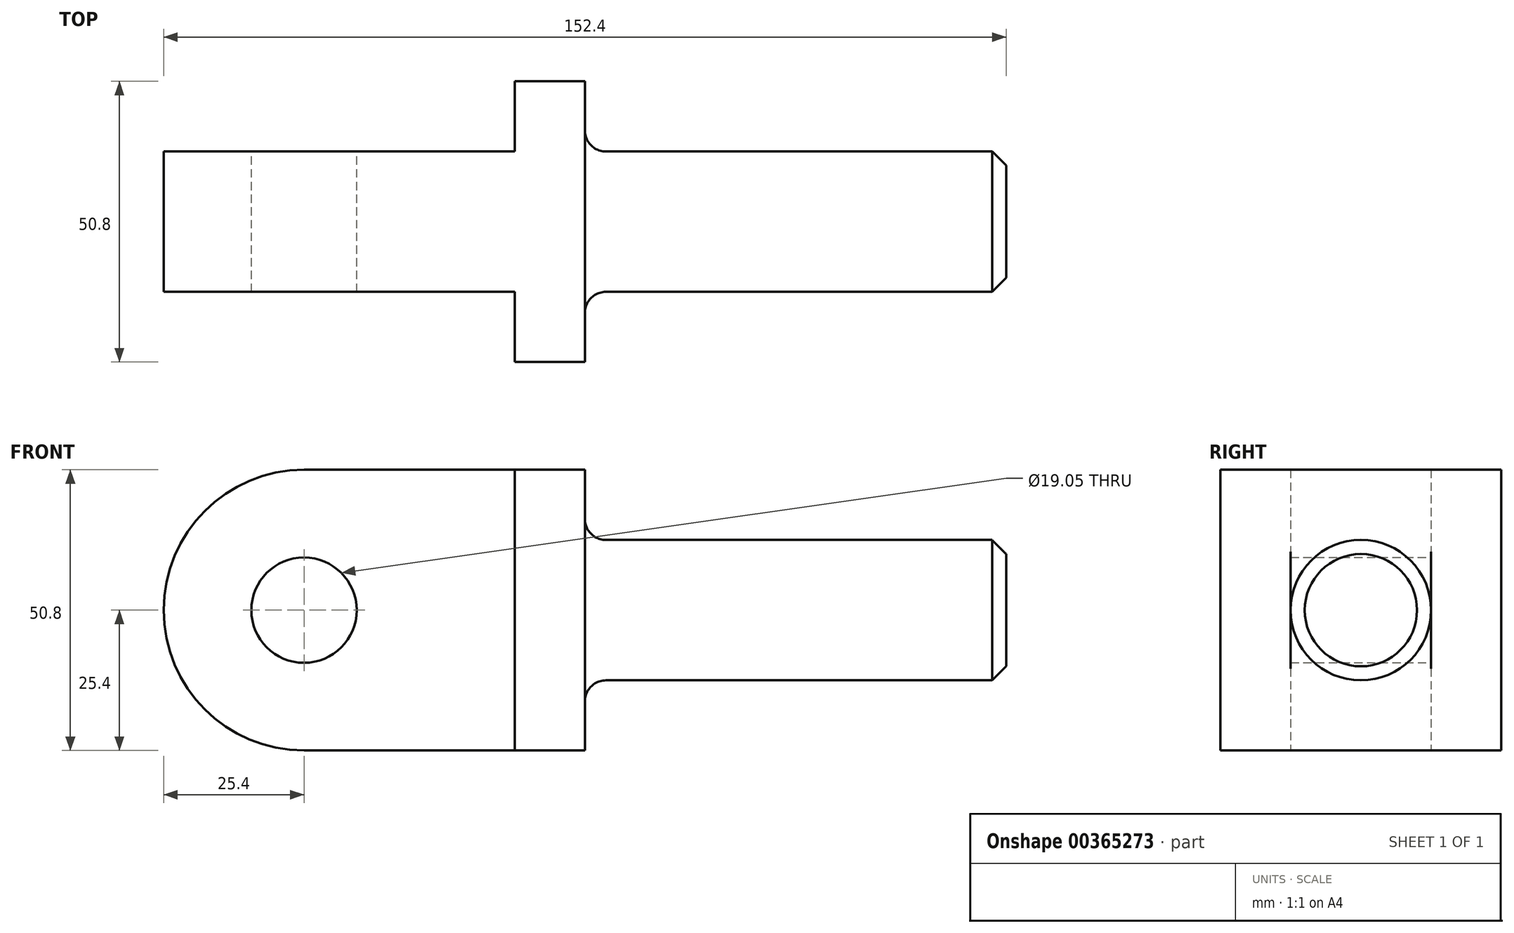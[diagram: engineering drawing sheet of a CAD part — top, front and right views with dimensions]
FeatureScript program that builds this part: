
annotation { "Feature Type Name" : "Feature", "Feature Type Description" : "" }
export const myFeature = defineFeature(function(context is Context, id is Id, definition is map)
    precondition{}
    {
        {
            var Q0;
            Q0=qCreatedBy(makeId("Front.planeOp"),FACE);
            var sketch = newSketch(context, id + "F0", { "sketchPlane" : qUnion([Q0])});
            skLineSegment(sketch, "E0.bottom", {"start": v(0, 0) * mm, "end": v(-12.7, 0) * mm});
            skLineSegment(sketch, "E0.top", {"start": v(0, 50.8) * mm, "end": v(-12.7, 50.8) * mm});
            skLineSegment(sketch, "E0.left", {"start": v(0, 0) * mm, "end": v(0, 50.8) * mm});
            skLineSegment(sketch, "E0.right", {"start": v(-12.7, 0) * mm, "end": v(-12.7, 50.8) * mm});
            skLineSegment(sketch, "E1", {"start": v(-12.7, 50.8) * mm, "end": v(-50.8, 50.8) * mm});
            skLineSegment(sketch, "E2", {"start": v(-12.7, 0) * mm, "end": v(-50.8, 0) * mm});
            skArc(sketch, "E3", {"start": v(-50.8, 50.8) * mm, "mid": v(-76.2, 25.4) * mm, "end": v(-50.8, 0) * mm});
            skCircle(sketch, "E4", {"center": v(-50.8, 25.4) * mm, "radius": 9.53 * mm});
            skSolve(sketch);
        }
        {
            var Q0;
            Q0=makeQuery(id+"F0.imprint","IMPRINT",FACE,{"disambiguationData":[TD([[makeQuery(id+"F0.imprint","IMPRINT",EDGE,{"derivedFrom":sQuery(id+"F0.wireOp",EDGE,"E0.right")}),1.0]])]});
            extrude(context, id + "F1", {"entities" : qUnion([Q0]), "endBound" : BoundingType.SYMMETRIC, "depth" : 25.4 * mm});
        }
        {
            var Q0;
            Q0=makeQuery(id+"F0.imprint","IMPRINT",FACE,{"disambiguationData":[TD([[makeQuery(id+"F0.imprint","IMPRINT",EDGE,{"derivedFrom":sQuery(id+"F0.wireOp",EDGE,"E0.bottom")}),-1.0]])]});
            extrude(context, id + "F2", {"entities" : qUnion([Q0]), "operationType" : NewBodyOperationType.ADD, "endBound" : BoundingType.SYMMETRIC, "depth" : 50.8 * mm});
        }
        {
            var Q0;
            Q0=qCreatedBy(makeId("Right.planeOp"),FACE);
            var sketch = newSketch(context, id + "F3", { "sketchPlane" : qUnion([Q0])});
            skCircle(sketch, "E5", {"center": v(0, 25.4) * mm, "radius": 12.7 * mm});
            skSolve(sketch);
        }
        {
            var Q0;
            Q0=qCreatedBy(makeId("Front.planeOp"),FACE);
            var sketch = newSketch(context, id + "F4", { "sketchPlane" : qUnion([Q0])});
            skLineSegment(sketch, "E6", {"start": v(0, 25.4) * mm, "end": v(76.2, 25.4) * mm});
            skLineSegment(sketch, "E7", {"start": v(76.2, 25.4) * mm, "end": v(76.2, 38.1) * mm});
            skLineSegment(sketch, "E8", {"start": v(76.2, 38.1) * mm, "end": v(3.81, 38.1) * mm});
            skArc(sketch, "E9", {"start": v(3.81, 38.1) * mm, "mid": v(1.12, 39.22) * mm, "end": v(0, 41.9) * mm});
            skLineSegment(sketch, "E10", {"start": v(0, 41.9) * mm, "end": v(0, 25.4) * mm});
            skLineSegment(sketch, "E11", {"start": v(0, 25.4) * mm, "end": v(88.17, 25.4) * mm, "construction": true});
            skSolve(sketch);
        }
        {
            var Q0;
            Q0 = qSketchRegion(id + "F4", true);
            var Q1;
            Q1=sQuery(id+"F4.wireOp",EDGE,"E11");
            revolve(context, id + "F5", {"operationType" : NewBodyOperationType.ADD, "entities" : qUnion([Q0]), "axis" : qUnion([Q1]), "revolveType" : RevolveType.FULL});
        }
        {
            var Q0;
            Q0=makeQuery(id+"F5.opRevolve","SWEPT_EDGE",EDGE,{"disambiguationData":[OSD([sQuery(id+"F4.wireOp",EDGE,"E7"),sQuery(id+"F4.wireOp",EDGE,"E8")])]});
            chamfer(context, id + "F6", {"entities" : qUnion([Q0]), "chamferType" : ChamferType.OFFSET_ANGLE, "width" : 2.54 * mm, "oppositeDirection" : false, "angle" : 45 * degree, "tangentPropagation" : true});
        }
    });
